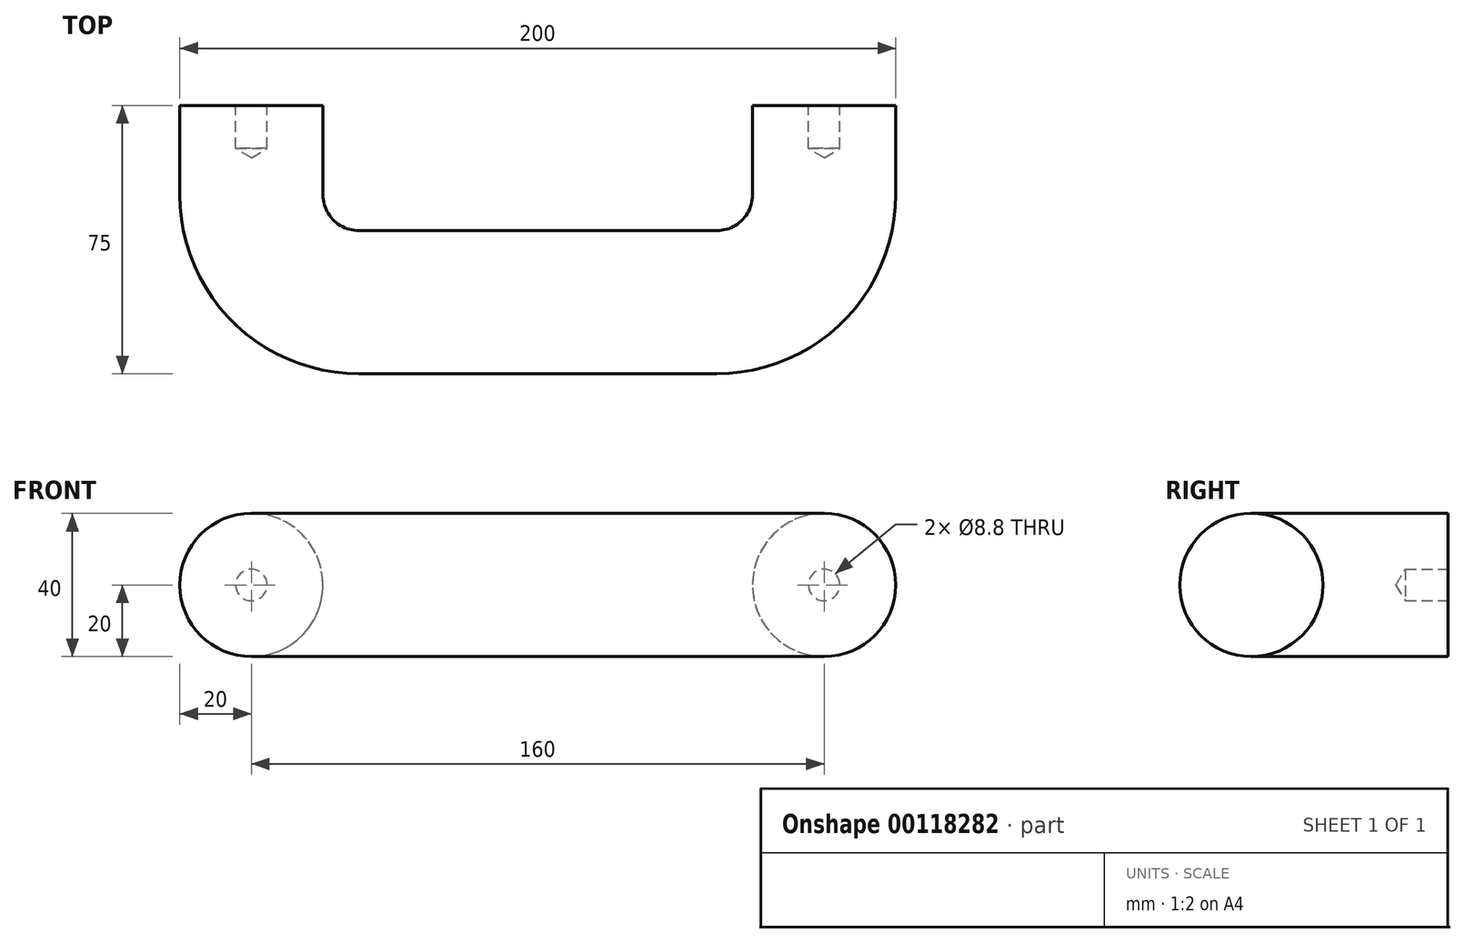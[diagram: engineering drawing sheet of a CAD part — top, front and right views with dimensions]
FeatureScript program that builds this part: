
annotation { "Feature Type Name" : "Feature", "Feature Type Description" : "" }
export const myFeature = defineFeature(function(context is Context, id is Id, definition is map)
    precondition{}
    {
        {
            var Q0;
            Q0=qCreatedBy(makeId("Front.planeOp"),FACE);
            var sketch = newSketch(context, id + "F0", { "sketchPlane" : qUnion([Q0])});
            skCircle(sketch, "E0", {"center": v(0, 0) * mm, "radius": 20 * mm});
            skSolve(sketch);
        }
        {
            var Q0;
            Q0=qCreatedBy(makeId("Top.planeOp"),FACE);
            var sketch = newSketch(context, id + "F1", { "sketchPlane" : qUnion([Q0])});
            skLineSegment(sketch, "E1", {"start": v(0, 0) * mm, "end": v(0, -25) * mm});
            skLineSegment(sketch, "E2", {"start": v(30, -55) * mm, "end": v(130, -55) * mm});
            skLineSegment(sketch, "E3", {"start": v(160, -25) * mm, "end": v(160, 0) * mm});
            skPoint(sketch, "E4.visualSharp", {"position": v(0, -55) * mm});
            skArc(sketch, "E4.filletArc", {"start": v(0, -25) * mm, "mid": v(8.79, -46.21) * mm, "end": v(30, -55) * mm});
            skPoint(sketch, "E5.visualSharp", {"position": v(160, -55) * mm});
            skArc(sketch, "E5.filletArc", {"start": v(130, -55) * mm, "mid": v(151.21, -46.21) * mm, "end": v(160, -25) * mm});
            skSolve(sketch);
        }
        {
            var Q0;
            Q0=makeQuery(id+"F0.imprint","IMPRINT",FACE,{"disambiguationData":[TD([[makeQuery(id+"F0.imprint","IMPRINT",EDGE,{"derivedFrom":sQuery(id+"F0.wireOp",EDGE,"E0")}),1.0]])]});
            var Q1;
            Q1=sQuery(id+"F1.wireOp",EDGE,"E1");
            var Q2;
            Q2=sQuery(id+"F1.wireOp",EDGE,"E4.filletArc");
            var Q3;
            Q3=sQuery(id+"F1.wireOp",EDGE,"E2");
            var Q4;
            Q4=sQuery(id+"F1.wireOp",EDGE,"E5.filletArc");
            var Q5;
            Q5=sQuery(id+"F1.wireOp",EDGE,"E3");
            sweep(context, id + "F2", {"profiles" : qUnion([Q0]), "path" : qUnion([Q1, Q2, Q3, Q4, Q5])});
        }
        {
            var Q0;
            Q0=makeQuery(id+"F2.opSweep","CAP_FACE",FACE,{"disambiguationData":[OSD([sQuery(id+"F0.wireOp",EDGE,"E0"),sQuery(id+"F1.wireOp",VERTEX,"E1.start")])],"isStart":true});
            var sketch = newSketch(context, id + "F3", { "sketchPlane" : qUnion([Q0])});
            skCircle(sketch, "E6.0.0", {"center": v(-160, 0) * mm, "radius": 20 * mm});
            skCircle(sketch, "E7.0.0", {"center": v(0, 0) * mm, "radius": 20 * mm});
            skLineSegment(sketch, "E8", {"start": v(0, 0) * mm, "end": v(-160, 0) * mm});
            skSolve(sketch);
        }
        {
            var Q0;
            Q0=sQuery(id+"F3.wireOp",VERTEX,"E7.0.0.center");
            var Q1;
            Q1=sQuery(id+"F3.wireOp",VERTEX,"E6.0.0.center");
            var Q2;
            Q2=makeQuery(id+"F2.opSweep","SWEPT_BODY",BODY,{"disambiguationData":[OSD([sQuery(id+"F0.wireOp",EDGE,"E0"),sQuery(id+"F1.wireOp",EDGE,"E3")])]});
            hole(context, id + "F4", {"style" : HoleStyle.SIMPLE, "endStyle" : HoleEndStyle.BLIND, "standardTappedOrClearance" : lookupTablePath({ "standard" : "ISO", "fit" : "Normal", "size" : "M8", "type" : "Clearance" }), "standardBlindInLast" : lookupTablePath({ "fit" : "Standard", "standard" : "ISO", "size" : "M8", "type" : "Clearance" }), "holeDiameter" : 8.8 * mm, "holeDepth" : 12 * mm, "locations" : qUnion([Q0, Q1]), "scope" : qUnion([Q2])});
        }
    });
